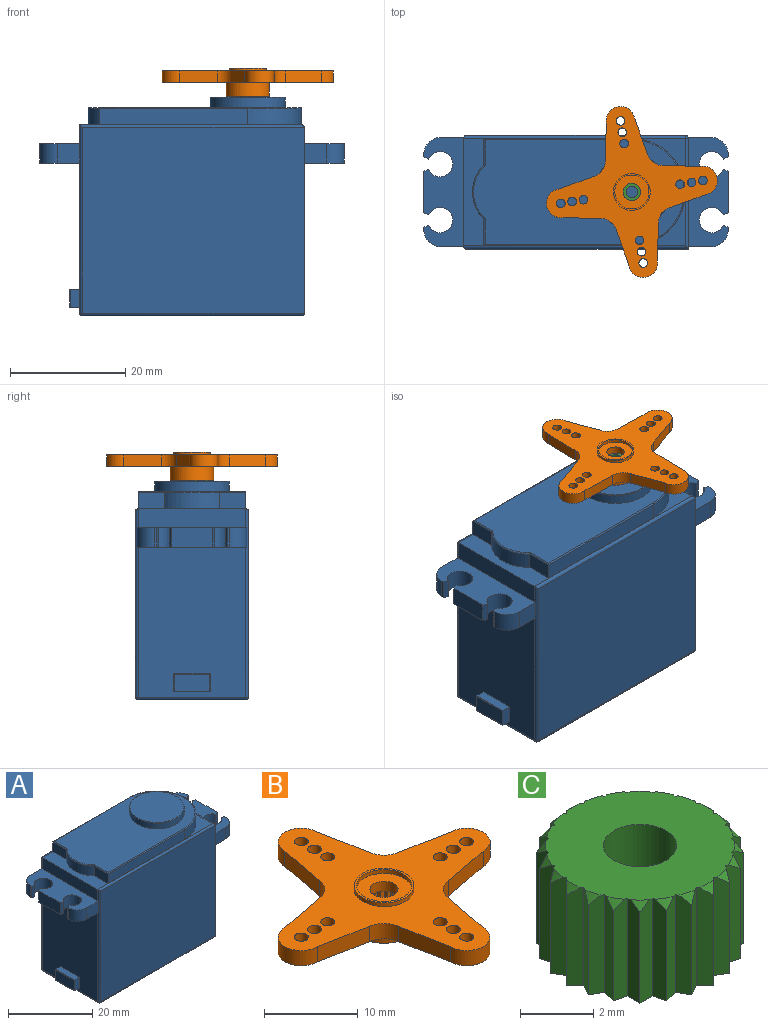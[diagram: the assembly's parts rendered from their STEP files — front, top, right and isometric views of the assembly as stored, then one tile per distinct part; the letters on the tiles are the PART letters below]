
ASSEMBLY  parts=3 mates=2
PART A: 76 faces, bbox 52.9x20.1x38 mm
  f0: plane 18.7x3.3mm, normal (-1,0,0), area 61.7mm2, adj f5,f10,f53,f56
  f1: plane 19x6.95mm, normal (0,0,1), area 94.6mm2, adj f2,f3,f4,f14,f17,f18,f19,f29
  f2: plane 3.34x0.38mm, normal (1,0,0), area 1.3mm2, adj f1,f9,f39,f42
  f3: plane 7.16x3.34mm, normal (1,0,0), area 23.9mm2, adj f1,f9,f37,f38
  f4: cylinder r=2.19mm len=4.38mm, axis (0,0,1), area 39.7mm2, adj f1,f9,f36,f37
  f5: plane 38.5x18.7mm, normal (0,0,1), area 93.1mm2, adj f0,f6,f30,f31,f32,f34,f35,f46
  f6: plane 4.61x2.8mm, normal (-1,0,0), area 12.9mm2, adj f5,f31,f34,f71
  f7: plane 3.34x0.38mm, normal (-1,0,0), area 1.3mm2, adj f10,f11,f26,f41
  f8: plane 7.16x3.34mm, normal (-1,0,0), area 23.9mm2, adj f10,f11,f23,f28
  f9: plane 19x6.95mm, normal (0,0,-1), area 94.6mm2, adj f2,f3,f4,f14,f17,f18,f19,f29
  f10: plane 19x6.95mm, normal (0,0,1), area 94.6mm2, adj f0,f7,f8,f20,f21,f22,f23,f24
  f11: plane 19x6.95mm, normal (0,0,-1), area 94.6mm2, adj f7,f8,f12,f20,f21,f22,f23,f24
  f12: plane 26.06x18.7mm, normal (-1,0,0), area 467.2mm2, adj f11,f53,f56,f59,f60,f61,f62,f63
  f13: plane 38x18.7mm, normal (0,0,-1), area 710.6mm2, adj f50,f54,f55,f59
  f14: plane 32.2x19.2mm, normal (1,0,0), area 555.3mm2, adj f1,f9,f15,f18,f46,f47,f50
  f15: plane 38.5x32.2mm, normal (0,-1,0), area 1239.7mm2, adj f14,f49,f53,f54
  f16: plane 38x32.2mm, normal (0,1,0), area 1223.6mm2, adj f47,f52,f55,f56
  f17: plane 3.34x0.38mm, normal (1,0,0), area 1.3mm2, adj f1,f9,f36,f43
  f18: plane 3.93x3.34mm, normal (0,-1,0), area 13.1mm2, adj f1,f9,f14,f42
  f19: plane 3.95x3.34mm, normal (0,1,0), area 13.2mm2, adj f1,f9,f43,f47
  f20: plane 3.95x3.34mm, normal (0,1,0), area 13.2mm2, adj f10,f11,f40,f56
  f21: plane 3.95x3.34mm, normal (0,-1,0), area 13.2mm2, adj f10,f11,f41,f53
  f22: plane 3.34x0.38mm, normal (-1,0,0), area 1.3mm2, adj f10,f11,f25,f40
  f23: plane 3.34x0.81mm, normal (-0.41,0.91,0), area 3mm2, adj f8,f10,f11,f24
  f24: cylinder r=2.19mm len=4.38mm, axis (0,0,1), area 39.7mm2, adj f10,f11,f23,f25
  f25: plane 3.34x0.81mm, normal (-0.41,-0.91,0), area 3mm2, adj f10,f11,f22,f24
  f26: plane 3.34x0.81mm, normal (-0.41,0.91,0), area 3mm2, adj f7,f10,f11,f27
  f27: cylinder r=2.19mm len=4.38mm, axis (0,0,1), area 39.7mm2, adj f10,f11,f26,f28
  f28: plane 3.34x0.81mm, normal (-0.41,-0.91,0), area 3mm2, adj f8,f10,f11,f27
  f29: cylinder r=2.19mm len=4.38mm, axis (0,0,1), area 39.7mm2, adj f1,f9,f38,f39
  f30: plane 25.7x2.8mm, normal (0,-1,0), area 72mm2, adj f5,f32,f35,f72
  f31: plane 25.7x2.8mm, normal (0,1,0), area 72mm2, adj f5,f6,f35,f73
  f32: plane 4.61x2.8mm, normal (-1,0,0), area 12.9mm2, adj f5,f30,f34,f70
  f33: plane 36.6x18.2mm, normal (0,0,1), area 474.2mm2, adj f44,f69,f70,f71,f72,f73,f74
  f34: cylinder r=6.5mm len=9.38mm, axis (0,0,1), area 29.3mm2, adj f5,f6,f32,f69
  f35: cylinder r=9.3mm len=18.6mm, axis (0,0,1), area 81.8mm2, adj f5,f30,f31,f74
  f36: plane 3.34x0.81mm, normal (0.41,-0.91,0), area 3mm2, adj f1,f4,f9,f17
  f37: plane 3.34x0.81mm, normal (0.41,0.91,0), area 3mm2, adj f1,f3,f4,f9
  f38: plane 3.34x0.81mm, normal (0.41,-0.91,0), area 3mm2, adj f1,f3,f9,f29
  f39: plane 3.34x0.81mm, normal (0.41,0.91,0), area 3mm2, adj f1,f2,f9,f29
  f40: cylinder r=3mm len=3.34mm, axis (0,0,1), area 15.7mm2, adj f10,f11,f20,f22
  f41: cylinder r=3mm len=3.34mm, axis (0,0,-1), area 15.7mm2, adj f7,f10,f11,f21
  f42: cylinder r=3mm len=3.34mm, axis (0,0,1), area 15.7mm2, adj f1,f2,f9,f18
  f43: cylinder r=3mm len=3.34mm, axis (0,0,-1), area 15.7mm2, adj f1,f9,f17,f19
  f44: cylinder r=6.5mm len=13mm, axis (0,0,-1), area 69.4mm2, adj f33,f75
  f45: plane 12.8x12.8mm, normal (0,0,1), area 128.7mm2, adj f75
  f46: cylinder r=0.5mm len=19.2mm, axis (0,1,0), area 14.9mm2, adj f5,f14,f48,f49
  f47: cylinder r=0.5mm len=32.2mm, axis (0,0,1), area 24.8mm2, adj f1,f9,f14,f16,f19,f48,f51
  f48: sphere r=0.5mm, area 0.4mm2, adj f46,f47,f52
  f49: cylinder r=0.5mm len=39mm, axis (1,0,0), area 30.3mm2, adj f5,f15,f46,f53
  f50: cylinder r=0.5mm len=19.2mm, axis (0,-1,0), area 14.9mm2, adj f13,f14,f51,f54
  f51: sphere r=0.5mm, area 0.4mm2, adj f47,f50,f55
  f52: cylinder r=0.5mm len=38.5mm, axis (-1,0,0), area 30.1mm2, adj f5,f16,f48,f56
  f53: cylinder r=0.5mm len=32.7mm, axis (0,0,1), area 25mm2, adj f0,f10,f11,f12,f15,f21,f49,f57
  f54: cylinder r=0.5mm len=38.5mm, axis (-1,0,0), area 30.1mm2, adj f13,f15,f50,f57
  f55: cylinder r=0.5mm len=38mm, axis (1,0,0), area 29.8mm2, adj f13,f16,f51,f58
  f56: cylinder r=0.5mm len=32.7mm, axis (0,0,-1), area 25mm2, adj f0,f10,f11,f12,f16,f20,f52,f58
  f57: sphere r=0.5mm, area 0.4mm2, adj f53,f54,f59
  f58: sphere r=0.5mm, area 0.4mm2, adj f55,f56,f59
  f59: cylinder r=0.5mm len=18.7mm, axis (0,1,0), area 14.7mm2, adj f12,f13,f57,f58
  f60: plane 6.4x1.65mm, normal (0,0,1), area 10.6mm2, adj f12,f61,f63,f65
  f61: plane 3.15x1.65mm, normal (0,1,0), area 5.2mm2, adj f12,f60,f62,f66
  f62: plane 6.4x1.65mm, normal (0,0,-1), area 10.6mm2, adj f12,f61,f63,f68
  f63: plane 3.15x1.65mm, normal (0,-1,0), area 5.2mm2, adj f12,f60,f62,f67
  f64: plane 6.2x2.95mm, normal (-1,0,0), area 18.3mm2, adj f65,f66,f67,f68
  f65: cylinder r=0.1mm len=6.4mm, axis (0,-1,0), area 1mm2, adj f60,f64,f66,f67
  f66: cylinder r=0.1mm len=3.15mm, axis (0,0,1), area 0.5mm2, adj f61,f64,f65,f68
  f67: cylinder r=0.1mm len=3.15mm, axis (0,0,-1), area 0.5mm2, adj f63,f64,f65,f68
  f68: cylinder r=0.1mm len=6.4mm, axis (0,1,0), area 1mm2, adj f62,f64,f66,f67
  f69: torus R=6.3mm, axis (0,0,1), area 3.3mm2, adj f33,f34,f70,f71
  f70: cylinder r=0.2mm len=4.7mm, axis (0,1,0), area 1.4mm2, adj f32,f33,f69,f72
  f71: cylinder r=0.2mm len=4.7mm, axis (0,1,0), area 1.4mm2, adj f6,f33,f69,f73
  f72: cylinder r=0.2mm len=25.7mm, axis (-1,0,0), area 8.1mm2, adj f30,f33,f70,f74
  f73: cylinder r=0.2mm len=25.7mm, axis (1,0,0), area 8.1mm2, adj f31,f33,f71,f74
  f74: torus R=9.1mm, axis (0,0,1), area 9.1mm2, adj f33,f35,f72,f73
  f75: torus R=6.4mm, axis (0,0,1), area 6.4mm2, adj f44,f45
PART B: 110 faces, bbox 30x30x4.9 mm
  f0: plane 7.52x7.52mm, normal (0,0,-1), area 22.2mm2, adj f36,f62,f63,f64,f65,f66,f67,f68
  f1: plane 5.9x5.9mm, normal (0,0,1), area 20.3mm2, adj f22,f33
  f2: plane 6.52x2mm, normal (0.18,0.98,0), area 13.3mm2, adj f3,f29,f31,f32
  f3: cylinder r=2.67mm len=2.26mm, axis (0,0,-1), area 6.8mm2, adj f2,f4,f31,f32
  f4: plane 6.52x2mm, normal (0.98,0.18,0), area 13.3mm2, adj f3,f5,f31,f32
  f5: cylinder r=2.5mm len=5mm, axis (0,0,-1), area 15.7mm2, adj f4,f6,f31,f32
  f6: plane 6.52x2mm, normal (-0.98,0.18,0), area 13.3mm2, adj f5,f7,f31,f32
  f7: cylinder r=2.67mm len=2.26mm, axis (0,0,-1), area 6.8mm2, adj f6,f8,f31,f32
  f8: plane 6.52x2mm, normal (-0.18,0.98,0), area 13.3mm2, adj f7,f9,f31,f32
  f9: cylinder r=2.5mm len=5mm, axis (0,0,-1), area 15.7mm2, adj f8,f10,f31,f32
  f10: plane 6.52x2mm, normal (-0.18,-0.98,0), area 13.3mm2, adj f9,f11,f31,f32
  f11: cylinder r=2.67mm len=2.26mm, axis (0,0,-1), area 6.8mm2, adj f10,f12,f31,f32
  f12: plane 6.52x2mm, normal (-0.98,-0.18,0), area 13.3mm2, adj f11,f13,f31,f32
  f13: cylinder r=2.5mm len=5mm, axis (0,0,-1), area 15.7mm2, adj f12,f14,f31,f32
  f14: plane 6.52x2mm, normal (0.98,-0.18,0), area 13.3mm2, adj f13,f15,f31,f32
  f15: cylinder r=2.67mm len=2.26mm, axis (0,0,-1), area 6.8mm2, adj f14,f16,f31,f32
  f16: plane 6.52x2mm, normal (0.18,-0.98,0), area 13.3mm2, adj f15,f29,f31,f32
  f17: cylinder r=0.75mm len=2mm, axis (0,0,-1), area 9.4mm2, adj f31,f32
  f18: cylinder r=0.75mm len=2mm, axis (0,0,-1), area 9.4mm2, adj f31,f32
  f19: cylinder r=0.75mm len=2mm, axis (0,0,-1), area 9.4mm2, adj f31,f32
  f20: cylinder r=0.75mm len=2mm, axis (0,0,-1), area 9.4mm2, adj f31,f32
  f21: cylinder r=0.75mm len=2mm, axis (0,0,-1), area 9.4mm2, adj f31,f32
  f22: cylinder r=1.5mm len=3mm, axis (0,0,-1), area 12.3mm2, adj f1,f37
  f23: cylinder r=0.75mm len=2mm, axis (0,0,-1), area 9.4mm2, adj f31,f32
  f24: cylinder r=0.75mm len=2mm, axis (0,0,-1), area 9.4mm2, adj f31,f32
  f25: cylinder r=0.75mm len=2mm, axis (0,0,-1), area 9.4mm2, adj f31,f32
  f26: cylinder r=0.75mm len=2mm, axis (0,0,-1), area 9.4mm2, adj f31,f32
  f27: cylinder r=0.75mm len=2mm, axis (0,0,-1), area 9.4mm2, adj f31,f32
  f28: cylinder r=0.75mm len=2mm, axis (0,0,-1), area 9.4mm2, adj f31,f32
  f29: cylinder r=2.5mm len=5mm, axis (0,0,-1), area 15.7mm2, adj f2,f16,f31,f32
  f30: cylinder r=0.75mm len=2mm, axis (0,0,-1), area 9.4mm2, adj f31,f32
  f31: plane 30x30mm, normal (0,0,1), area 276.6mm2, adj f2,f3,f4,f5,f6,f7,f8,f9
  f32: plane 30x30mm, normal (0,0,-1), area 264.3mm2, adj f2,f3,f4,f5,f6,f7,f8,f9
  f33: cylinder r=2.95mm len=5.9mm, axis (0,0,-1), area 9.3mm2, adj f1,f35
  f34: cylinder r=3.2mm len=6.4mm, axis (0,0,-1), area 10.1mm2, adj f31,f35
  f35: plane 6.4x6.4mm, normal (0,0,1), area 4.8mm2, adj f33,f34
  f36: cylinder r=3.76mm len=7.52mm, axis (0,0,1), area 56.7mm2, adj f0,f32
  f37: plane 5.15x5.15mm, normal (0,0,-1), area 13.6mm2, adj f22,f38,f39,f40,f41,f42,f43,f44
  f38: cone r=2.58mm half-angle=45deg, axis (0,0,-1), area 0.1mm2, adj f37,f86,f109
  f39: cone r=2.58mm half-angle=45deg, axis (0,0,-1), area 0.1mm2, adj f37,f82,f106
  f40: cone r=2.58mm half-angle=45deg, axis (0,0,-1), area 0.1mm2, adj f37,f62,f105
  f41: cone r=2.58mm half-angle=45deg, axis (0,0,-1), area 0.1mm2, adj f37,f80,f103
  f42: cone r=2.58mm half-angle=45deg, axis (0,0,-1), area 0.1mm2, adj f37,f78,f101
  f43: cone r=2.58mm half-angle=45deg, axis (0,0,-1), area 0.1mm2, adj f37,f76,f99
  f44: cone r=2.58mm half-angle=45deg, axis (0,0,-1), area 0.1mm2, adj f37,f64,f97
  f45: cone r=2.58mm half-angle=45deg, axis (0,0,-1), area 0.1mm2, adj f37,f66,f95
  f46: cone r=2.58mm half-angle=45deg, axis (0,0,-1), area 0.1mm2, adj f37,f68,f93
  f47: cone r=2.58mm half-angle=45deg, axis (0,0,-1), area 0.1mm2, adj f37,f70,f91
  f48: cone r=2.58mm half-angle=45deg, axis (0,0,-1), area 0.1mm2, adj f37,f72,f89
  f49: cone r=2.58mm half-angle=45deg, axis (0,0,-1), area 0.1mm2, adj f37,f74,f87
  f50: cone r=2.58mm half-angle=45deg, axis (0,0,-1), area 0.1mm2, adj f37,f85,f108
  f51: cone r=2.58mm half-angle=45deg, axis (0,0,-1), area 0.1mm2, adj f37,f83,f104
  f52: cone r=2.58mm half-angle=45deg, axis (0,0,-1), area 0.1mm2, adj f37,f81,f100
  f53: cone r=2.58mm half-angle=45deg, axis (0,0,-1), area 0.1mm2, adj f37,f79,f98
  f54: cone r=2.58mm half-angle=45deg, axis (0,0,-1), area 0.1mm2, adj f37,f77,f96
  f55: cone r=2.58mm half-angle=45deg, axis (0,0,-1), area 0.1mm2, adj f37,f75,f107
  f56: cone r=2.58mm half-angle=45deg, axis (0,0,-1), area 0.1mm2, adj f37,f73,f84
  f57: cone r=2.58mm half-angle=45deg, axis (0,0,-1), area 0.1mm2, adj f37,f71,f88
  f58: cone r=2.58mm half-angle=45deg, axis (0,0,-1), area 0.1mm2, adj f37,f69,f90
  f59: cone r=2.58mm half-angle=45deg, axis (0,0,-1), area 0.1mm2, adj f37,f67,f92
  f60: cone r=2.58mm half-angle=45deg, axis (0,0,-1), area 0.1mm2, adj f37,f65,f94
  f61: cone r=2.58mm half-angle=45deg, axis (0,0,-1), area 0.1mm2, adj f37,f63,f102
  f62: plane 3.12x0.47mm, normal (-0.25,0.97,0), area 1.4mm2, adj f0,f37,f40,f63,f105
  f63: plane 3.12x0.49mm, normal (-1,-0.01,0), area 1.4mm2, adj f0,f37,f61,f62,f102
  f64: plane 3.12x0.47mm, normal (0.96,-0.27,0), area 1.4mm2, adj f0,f37,f44,f65,f97
  f65: plane 3.12x0.43mm, normal (0.49,0.87,0), area 1.4mm2, adj f0,f37,f60,f64,f94
  f66: plane 3.12x0.35mm, normal (0.7,-0.72,0), area 1.4mm2, adj f0,f37,f45,f67,f95
  f67: plane 3.12x0.42mm, normal (0.86,0.51,0), area 1.4mm2, adj f0,f37,f59,f66,f92
  f68: plane 3.12x0.47mm, normal (0.25,-0.97,0), area 1.4mm2, adj f0,f37,f46,f69,f93
  f69: plane 3.12x0.49mm, normal (1,0.01,0), area 1.4mm2, adj f0,f37,f58,f68,f90
  f70: plane 3.12x0.47mm, normal (-0.27,-0.96,0), area 1.4mm2, adj f0,f37,f47,f71,f91
  f71: plane 3.12x0.43mm, normal (0.87,-0.49,0), area 1.4mm2, adj f0,f37,f57,f70,f88
  f72: plane 3.12x0.35mm, normal (-0.72,-0.7,0), area 1.4mm2, adj f0,f37,f48,f73,f89
  f73: plane 3.12x0.42mm, normal (0.51,-0.86,0), area 1.4mm2, adj f0,f37,f56,f72,f84
  f74: plane 3.12x0.47mm, normal (-0.96,0.27,0), area 1.4mm2, adj f0,f37,f49,f75,f87
  f75: plane 3.12x0.43mm, normal (-0.49,-0.87,0), area 1.4mm2, adj f0,f37,f55,f74,f107
  f76: plane 3.12x0.47mm, normal (0.97,0.25,0), area 1.4mm2, adj f0,f37,f43,f77,f99
  f77: plane 3.12x0.49mm, normal (-0.01,1,0), area 1.4mm2, adj f0,f37,f54,f76,f96
  f78: plane 3.12x0.35mm, normal (0.72,0.7,0), area 1.4mm2, adj f0,f37,f42,f79,f101
  f79: plane 3.12x0.42mm, normal (-0.51,0.86,0), area 1.4mm2, adj f0,f37,f53,f78,f98
  f80: plane 3.12x0.47mm, normal (0.27,0.96,0), area 1.4mm2, adj f0,f37,f41,f81,f103
  f81: plane 3.12x0.43mm, normal (-0.87,0.49,0), area 1.4mm2, adj f0,f37,f52,f80,f100
  f82: plane 3.12x0.35mm, normal (-0.7,0.72,0), area 1.4mm2, adj f0,f37,f39,f83,f106
  f83: plane 3.12x0.42mm, normal (-0.86,-0.51,0), area 1.4mm2, adj f0,f37,f51,f82,f104
  f84: plane 3.12x0.43mm, normal (-0.87,-0.49,0), area 1.4mm2, adj f0,f37,f56,f73,f85
  f85: plane 3.12x0.47mm, normal (0.27,-0.96,0), area 1.4mm2, adj f0,f37,f50,f84,f108
  f86: plane 3.12x0.49mm, normal (-1,0.01,0), area 1.4mm2, adj f0,f37,f38,f87,f109
  f87: plane 3.12x0.47mm, normal (-0.25,-0.97,0), area 1.4mm2, adj f0,f37,f49,f74,f86
  f88: plane 3.12x0.42mm, normal (-0.51,-0.86,0), area 1.4mm2, adj f0,f37,f57,f71,f89
  f89: plane 3.12x0.35mm, normal (0.72,-0.7,0), area 1.4mm2, adj f0,f37,f48,f72,f88
  f90: plane 3.12x0.49mm, normal (-0.01,-1,0), area 1.4mm2, adj f0,f37,f58,f69,f91
  f91: plane 3.12x0.47mm, normal (0.97,-0.25,0), area 1.4mm2, adj f0,f37,f47,f70,f90
  f92: plane 3.12x0.43mm, normal (0.49,-0.87,0), area 1.4mm2, adj f0,f37,f59,f67,f93
  f93: plane 3.12x0.47mm, normal (0.96,0.27,0), area 1.4mm2, adj f0,f37,f46,f68,f92
  f94: plane 3.12x0.42mm, normal (0.86,-0.51,0), area 1.4mm2, adj f0,f37,f60,f65,f95
  f95: plane 3.12x0.35mm, normal (0.7,0.72,0), area 1.4mm2, adj f0,f37,f45,f66,f94
  f96: plane 3.12x0.49mm, normal (1,-0.01,0), area 1.4mm2, adj f0,f37,f54,f77,f97
  f97: plane 3.12x0.47mm, normal (0.25,0.97,0), area 1.4mm2, adj f0,f37,f44,f64,f96
  f98: plane 3.12x0.43mm, normal (0.87,0.49,0), area 1.4mm2, adj f0,f37,f53,f79,f99
  f99: plane 3.12x0.47mm, normal (-0.27,0.96,0), area 1.4mm2, adj f0,f37,f43,f76,f98
  f100: plane 3.12x0.42mm, normal (0.51,0.86,0), area 1.4mm2, adj f0,f37,f52,f81,f101
  f101: plane 3.12x0.35mm, normal (-0.72,0.7,0), area 1.4mm2, adj f0,f37,f42,f78,f100
  f102: plane 3.12x0.49mm, normal (0.01,1,0), area 1.4mm2, adj f0,f37,f61,f63,f103
  f103: plane 3.12x0.47mm, normal (-0.97,0.25,0), area 1.4mm2, adj f0,f37,f41,f80,f102
  f104: plane 3.12x0.43mm, normal (-0.49,0.87,0), area 1.4mm2, adj f0,f37,f51,f83,f105
  f105: plane 3.12x0.47mm, normal (-0.96,-0.27,0), area 1.4mm2, adj f0,f37,f40,f62,f104
  f106: plane 3.12x0.35mm, normal (-0.7,-0.72,0), area 1.4mm2, adj f0,f37,f39,f82,f107
  f107: plane 3.12x0.42mm, normal (-0.86,0.51,0), area 1.4mm2, adj f0,f37,f55,f75,f106
  f108: plane 3.12x0.47mm, normal (-0.97,-0.25,0), area 1.4mm2, adj f0,f37,f50,f85,f109
  f109: plane 3.12x0.49mm, normal (0.01,-1,0), area 1.4mm2, adj f0,f37,f38,f86,f108
PART C: 75 faces, bbox 5.7x5.7x3.3 mm
  f0: cone r=2.58mm half-angle=45deg, axis (0,0,-1), area 0.1mm2, adj f2,f51,f74
  f1: cone r=2.58mm half-angle=45deg, axis (0,0,-1), area 0.1mm2, adj f2,f47,f71
  f2: plane 5.15x5.15mm, normal (0,0,1), area 17.6mm2, adj f0,f1,f4,f5,f6,f7,f8,f9
  f3: plane 5.65x5.65mm, normal (0,0,-1), area 19.1mm2, adj f25,f27,f28,f29,f30,f31,f32,f33
  f4: cone r=2.58mm half-angle=45deg, axis (0,0,-1), area 0.1mm2, adj f2,f27,f70
  f5: cone r=2.58mm half-angle=45deg, axis (0,0,-1), area 0.1mm2, adj f2,f45,f68
  f6: cone r=2.58mm half-angle=45deg, axis (0,0,-1), area 0.1mm2, adj f2,f43,f66
  f7: cone r=2.58mm half-angle=45deg, axis (0,0,-1), area 0.1mm2, adj f2,f41,f64
  f8: cone r=2.58mm half-angle=45deg, axis (0,0,-1), area 0.1mm2, adj f2,f29,f62
  f9: cone r=2.58mm half-angle=45deg, axis (0,0,-1), area 0.1mm2, adj f2,f31,f60
  f10: cone r=2.58mm half-angle=45deg, axis (0,0,-1), area 0.1mm2, adj f2,f33,f58
  f11: cone r=2.58mm half-angle=45deg, axis (0,0,-1), area 0.1mm2, adj f2,f35,f56
  f12: cone r=2.58mm half-angle=45deg, axis (0,0,-1), area 0.1mm2, adj f2,f37,f54
  f13: cone r=2.58mm half-angle=45deg, axis (0,0,-1), area 0.1mm2, adj f2,f39,f52
  f14: cone r=2.58mm half-angle=45deg, axis (0,0,-1), area 0.1mm2, adj f2,f50,f73
  f15: cone r=2.58mm half-angle=45deg, axis (0,0,-1), area 0.1mm2, adj f2,f48,f69
  f16: cone r=2.58mm half-angle=45deg, axis (0,0,-1), area 0.1mm2, adj f2,f46,f65
  f17: cone r=2.58mm half-angle=45deg, axis (0,0,-1), area 0.1mm2, adj f2,f44,f63
  f18: cone r=2.58mm half-angle=45deg, axis (0,0,-1), area 0.1mm2, adj f2,f42,f61
  f19: cone r=2.58mm half-angle=45deg, axis (0,0,-1), area 0.1mm2, adj f2,f40,f72
  f20: cone r=2.58mm half-angle=45deg, axis (0,0,-1), area 0.1mm2, adj f2,f38,f49
  f21: cone r=2.58mm half-angle=45deg, axis (0,0,-1), area 0.1mm2, adj f2,f36,f53
  f22: cone r=2.58mm half-angle=45deg, axis (0,0,-1), area 0.1mm2, adj f2,f34,f55
  f23: cone r=2.58mm half-angle=45deg, axis (0,0,-1), area 0.1mm2, adj f2,f32,f57
  f24: cone r=2.58mm half-angle=45deg, axis (0,0,-1), area 0.1mm2, adj f2,f30,f59
  f25: cylinder r=1mm len=3.26mm, axis (0,0,-1), area 20.5mm2, adj f2,f3
  f26: cone r=2.58mm half-angle=45deg, axis (0,0,-1), area 0.1mm2, adj f2,f28,f67
  f27: plane 3.28x0.47mm, normal (0.25,-0.97,0), area 1.5mm2, adj f2,f3,f4,f28,f70
  f28: plane 3.28x0.49mm, normal (1,0.01,0), area 1.5mm2, adj f2,f3,f26,f27,f67
  f29: plane 3.28x0.47mm, normal (-0.96,0.27,0), area 1.5mm2, adj f2,f3,f8,f30,f62
  f30: plane 3.28x0.43mm, normal (-0.49,-0.87,0), area 1.5mm2, adj f2,f3,f24,f29,f59
  f31: plane 3.28x0.35mm, normal (-0.7,0.72,0), area 1.5mm2, adj f2,f3,f9,f32,f60
  f32: plane 3.28x0.42mm, normal (-0.86,-0.51,0), area 1.5mm2, adj f2,f3,f23,f31,f57
  f33: plane 3.28x0.47mm, normal (-0.25,0.97,0), area 1.5mm2, adj f2,f3,f10,f34,f58
  f34: plane 3.28x0.49mm, normal (-1,-0.01,0), area 1.5mm2, adj f2,f3,f22,f33,f55
  f35: plane 3.28x0.47mm, normal (0.27,0.96,0), area 1.5mm2, adj f2,f3,f11,f36,f56
  f36: plane 3.28x0.43mm, normal (-0.87,0.49,0), area 1.5mm2, adj f2,f3,f21,f35,f53
  f37: plane 3.28x0.35mm, normal (0.72,0.7,0), area 1.5mm2, adj f2,f3,f12,f38,f54
  f38: plane 3.28x0.42mm, normal (-0.51,0.86,0), area 1.5mm2, adj f2,f3,f20,f37,f49
  f39: plane 3.28x0.47mm, normal (0.96,-0.27,0), area 1.5mm2, adj f2,f3,f13,f40,f52
  f40: plane 3.28x0.43mm, normal (0.49,0.87,0), area 1.5mm2, adj f2,f3,f19,f39,f72
  f41: plane 3.28x0.47mm, normal (-0.97,-0.25,0), area 1.5mm2, adj f2,f3,f7,f42,f64
  f42: plane 3.28x0.49mm, normal (0.01,-1,0), area 1.5mm2, adj f2,f3,f18,f41,f61
  f43: plane 3.28x0.35mm, normal (-0.72,-0.7,0), area 1.5mm2, adj f2,f3,f6,f44,f66
  f44: plane 3.28x0.42mm, normal (0.51,-0.86,0), area 1.5mm2, adj f2,f3,f17,f43,f63
  f45: plane 3.28x0.47mm, normal (-0.27,-0.96,0), area 1.5mm2, adj f2,f3,f5,f46,f68
  f46: plane 3.28x0.43mm, normal (0.87,-0.49,0), area 1.5mm2, adj f2,f3,f16,f45,f65
  f47: plane 3.28x0.35mm, normal (0.7,-0.72,0), area 1.5mm2, adj f1,f2,f3,f48,f71
  f48: plane 3.28x0.42mm, normal (0.86,0.51,0), area 1.5mm2, adj f2,f3,f15,f47,f69
  f49: plane 3.28x0.43mm, normal (0.87,0.49,0), area 1.5mm2, adj f2,f3,f20,f38,f50
  f50: plane 3.28x0.47mm, normal (-0.27,0.96,0), area 1.5mm2, adj f2,f3,f14,f49,f73
  f51: plane 3.28x0.49mm, normal (1,-0.01,0), area 1.5mm2, adj f0,f2,f3,f52,f74
  f52: plane 3.28x0.47mm, normal (0.25,0.97,0), area 1.5mm2, adj f2,f3,f13,f39,f51
  f53: plane 3.28x0.42mm, normal (0.51,0.86,0), area 1.5mm2, adj f2,f3,f21,f36,f54
  f54: plane 3.28x0.35mm, normal (-0.72,0.7,0), area 1.5mm2, adj f2,f3,f12,f37,f53
  f55: plane 3.28x0.49mm, normal (0.01,1,0), area 1.5mm2, adj f2,f3,f22,f34,f56
  f56: plane 3.28x0.47mm, normal (-0.97,0.25,0), area 1.5mm2, adj f2,f3,f11,f35,f55
  f57: plane 3.28x0.43mm, normal (-0.49,0.87,0), area 1.5mm2, adj f2,f3,f23,f32,f58
  f58: plane 3.28x0.47mm, normal (-0.96,-0.27,0), area 1.5mm2, adj f2,f3,f10,f33,f57
  f59: plane 3.28x0.42mm, normal (-0.86,0.51,0), area 1.5mm2, adj f2,f3,f24,f30,f60
  f60: plane 3.28x0.35mm, normal (-0.7,-0.72,0), area 1.5mm2, adj f2,f3,f9,f31,f59
  f61: plane 3.28x0.49mm, normal (-1,0.01,0), area 1.5mm2, adj f2,f3,f18,f42,f62
  f62: plane 3.28x0.47mm, normal (-0.25,-0.97,0), area 1.5mm2, adj f2,f3,f8,f29,f61
  f63: plane 3.28x0.43mm, normal (-0.87,-0.49,0), area 1.5mm2, adj f2,f3,f17,f44,f64
  f64: plane 3.28x0.47mm, normal (0.27,-0.96,0), area 1.5mm2, adj f2,f3,f7,f41,f63
  f65: plane 3.28x0.42mm, normal (-0.51,-0.86,0), area 1.5mm2, adj f2,f3,f16,f46,f66
  f66: plane 3.28x0.35mm, normal (0.72,-0.7,0), area 1.5mm2, adj f2,f3,f6,f43,f65
  f67: plane 3.28x0.49mm, normal (-0.01,-1,0), area 1.5mm2, adj f2,f3,f26,f28,f68
  f68: plane 3.28x0.47mm, normal (0.97,-0.25,0), area 1.5mm2, adj f2,f3,f5,f45,f67
  f69: plane 3.28x0.43mm, normal (0.49,-0.87,0), area 1.5mm2, adj f2,f3,f15,f48,f70
  f70: plane 3.28x0.47mm, normal (0.96,0.27,0), area 1.5mm2, adj f2,f3,f4,f27,f69
  f71: plane 3.28x0.35mm, normal (0.7,0.72,0), area 1.5mm2, adj f1,f2,f3,f47,f72
  f72: plane 3.28x0.42mm, normal (0.86,-0.51,0), area 1.5mm2, adj f2,f3,f19,f40,f71
  f73: plane 3.28x0.47mm, normal (0.97,0.25,0), area 1.5mm2, adj f2,f3,f14,f50,f74
  f74: plane 3.28x0.49mm, normal (-0.01,1,0), area 1.5mm2, adj f0,f2,f3,f51,f73
PLACE A at identity fixed
PLACE B rot(axis=(0,0,-1),80.9deg) t=(0,0,14)mm
PLACE C rot(axis=(0,0,-1),80.9deg) t=(0,0,0)mm
MATE revolute C.f25 <-> A.f44  axis (0,0,-1) through (0,0,11.44)mm
MATE fastened C.f25 <-> B.f22  axis (0,0,1) through (0,0,14.7)mm
